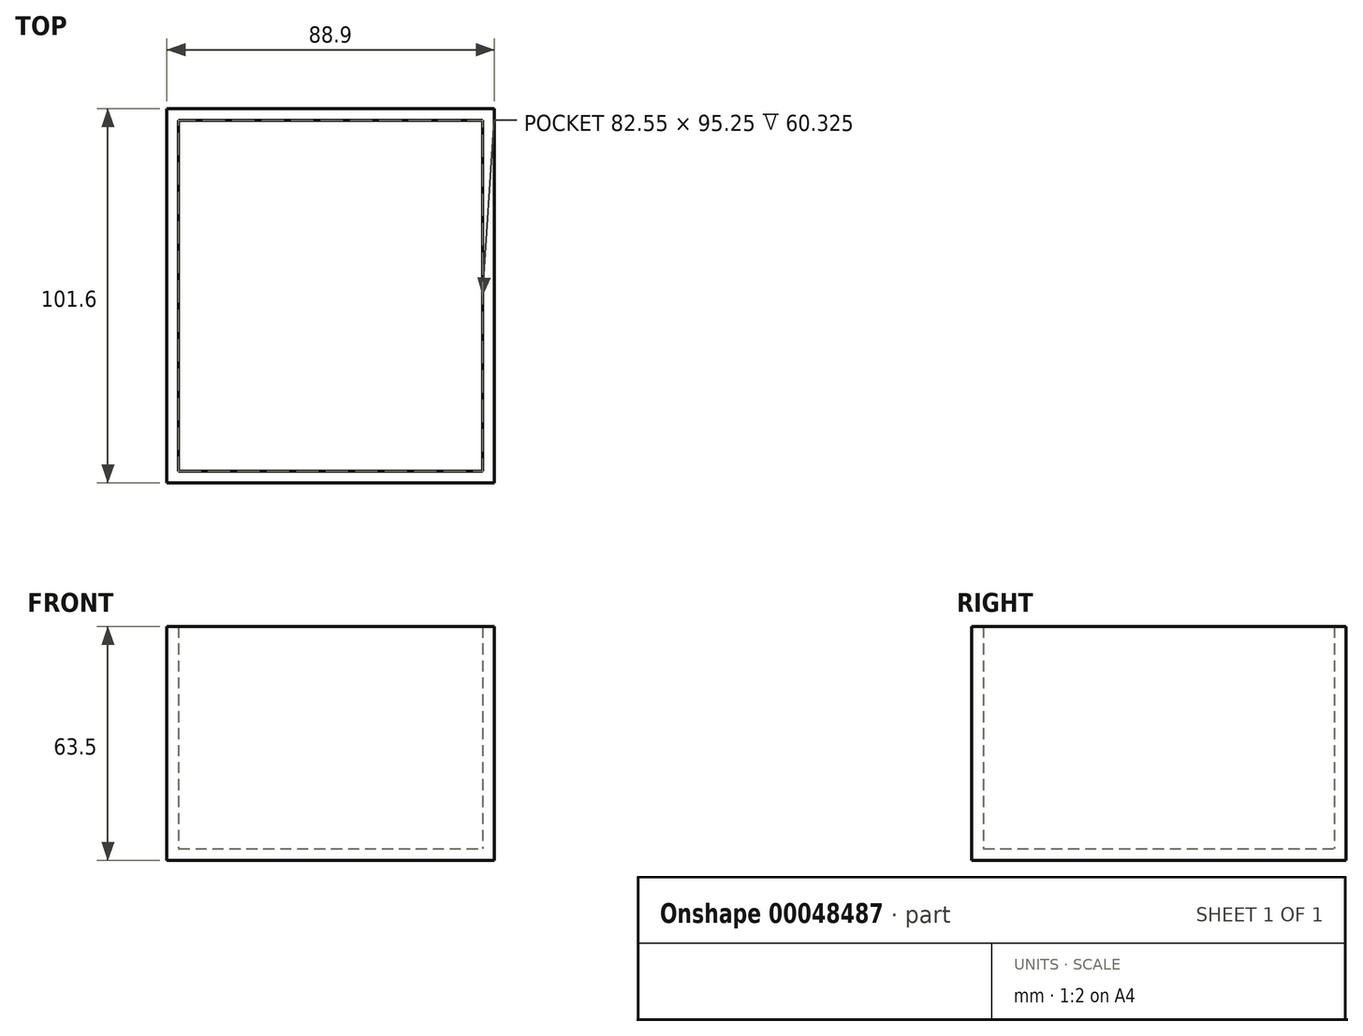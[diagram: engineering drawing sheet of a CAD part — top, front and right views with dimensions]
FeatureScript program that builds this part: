
annotation { "Feature Type Name" : "Feature", "Feature Type Description" : "" }
export const myFeature = defineFeature(function(context is Context, id is Id, definition is map)
    precondition{}
    {
        {
            var Q0;
            Q0=qCreatedBy(makeId("Front.planeOp"),FACE);
            var sketch = newSketch(context, id + "F0", { "sketchPlane" : qUnion([Q0])});
            skLineSegment(sketch, "E0.rect.bottom", {"start": v(-44.45, 31.75) * mm, "end": v(44.45, 31.75) * mm});
            skLineSegment(sketch, "E0.rect.top", {"start": v(-44.45, -31.75) * mm, "end": v(44.45, -31.75) * mm});
            skLineSegment(sketch, "E0.rect.left", {"start": v(-44.45, 31.75) * mm, "end": v(-44.45, -31.75) * mm});
            skLineSegment(sketch, "E0.rect.right", {"start": v(44.45, 31.75) * mm, "end": v(44.45, -31.75) * mm});
            skPoint(sketch, "E0.rect.middle", {"position": v(0, 0) * mm});
            skSolve(sketch);
        }
        {
            var Q0;
            Q0=makeQuery(id+"F0.imprint","IMPRINT",FACE,{"disambiguationData":[TD([[makeQuery(id+"F0.imprint","IMPRINT",EDGE,{"derivedFrom":sQuery(id+"F0.wireOp",EDGE,"E0.rect.bottom")}),-1.0]])]});
            extrude(context, id + "F1", {"entities" : qUnion([Q0]), "depth" : 101.6 * mm});
        }
        {
            var Q0;
            Q0=makeQuery(id+"F1.opExtrude","SWEPT_FACE",FACE,{"disambiguationData":[OSD([sQuery(id+"F0.wireOp",EDGE,"E0.rect.bottom")])]});
            shell(context, id + "F2", {"entities" : qUnion([Q0]), "thickness" : 3.17 * mm});
        }
    });
